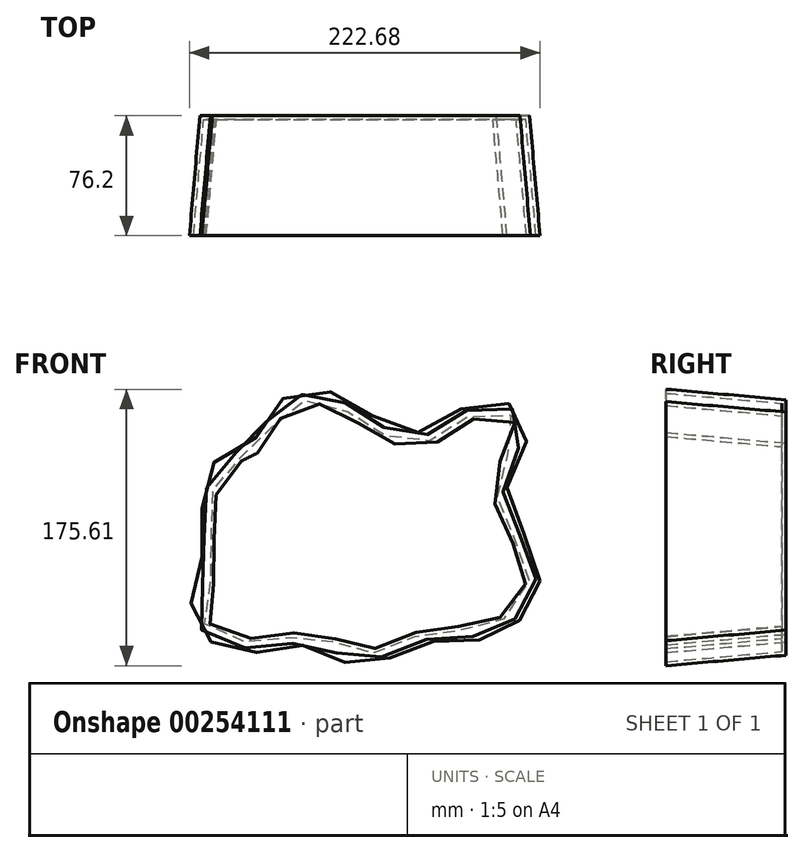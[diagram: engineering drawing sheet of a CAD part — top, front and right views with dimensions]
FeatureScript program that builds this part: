
annotation { "Feature Type Name" : "Feature", "Feature Type Description" : "" }
export const myFeature = defineFeature(function(context is Context, id is Id, definition is map)
    precondition{}
    {
        {
            var Q0;
            Q0=qCreatedBy(makeId("Front.planeOp"),FACE);
            var sketch = newSketch(context, id + "F0", { "sketchPlane" : qUnion([Q0])});
            skPoint(sketch, "E0.middle", {"position": v(0, 0) * mm});
            skPoint(sketch, "E1.visualSharp", {"position": v(-76.2, 50.8) * mm});
            skPoint(sketch, "E2.visualSharp", {"position": v(76.2, 50.8) * mm});
            skPoint(sketch, "E3.visualSharp", {"position": v(-76.2, -50.8) * mm});
            skPoint(sketch, "E4.visualSharp", {"position": v(76.2, -50.8) * mm});
            skPoint(sketch, "E5.14.internal.snap0", {"position": v(-76.2, 0) * mm});
            skFitSpline(sketch, "E6", {"points": [v(-86.3, 19.52) * mm, v(-82.18, 46.92) * mm, v(-52.14, 66.07) * mm, v(-48.01, 78.44) * mm, v(-20.03, 92.88) * mm, v(27.7, 68.13) * mm, v(59.22, 70.2) * mm, v(80.43, 83.74) * mm, v(108.41, 78.44) * mm, v(93.98, 37.2) * mm, v(114.9, -22.02) * mm, v(86.02, -52.07) * mm, v(52.44, -54.13) * mm, v(4.42, -69.16) * mm, v(-17.08, -56.78) * mm, v(-61.27, -60.9) * mm, v(-93.97, -45.3) * mm, v(-88.37, -24.38) * mm, v(-87.2, 0) * mm, v(-87.78, 3.02) * mm, v(-86.3, 19.52) * mm]});
            skPoint(sketch, "E7.orphan", {"position": v(-76.2, 25.4) * mm});
            skPoint(sketch, "E3.filletArc.start.orphan", {"position": v(-76.2, -25.4) * mm});
            skSolve(sketch);
        }
        {
            var Q0;
            Q0=makeQuery(id+"F0.imprint","IMPRINT",FACE,{"disambiguationData":[TD([[makeQuery(id+"F0.imprint","IMPRINT",EDGE,{"derivedFrom":sQuery(id+"F0.wireOp",EDGE,"E6")}),-1.0]])]});
            extrude(context, id + "F1", {"entities" : qUnion([Q0]), "depth" : 76.2 * mm, "hasDraft" : true, "draftAngle" : 5 * degree});
        }
        {
            var Q0;
            Q0=makeQuery(id+"F1.opExtrude","CAP_FACE",FACE,{"disambiguationData":[OSD([sQuery(id+"F0.wireOp",EDGE,"E6")])],"isStart":false});
            shell(context, id + "F2", {"entities" : qUnion([Q0]), "thickness" : 2.54 * mm});
        }
    });
